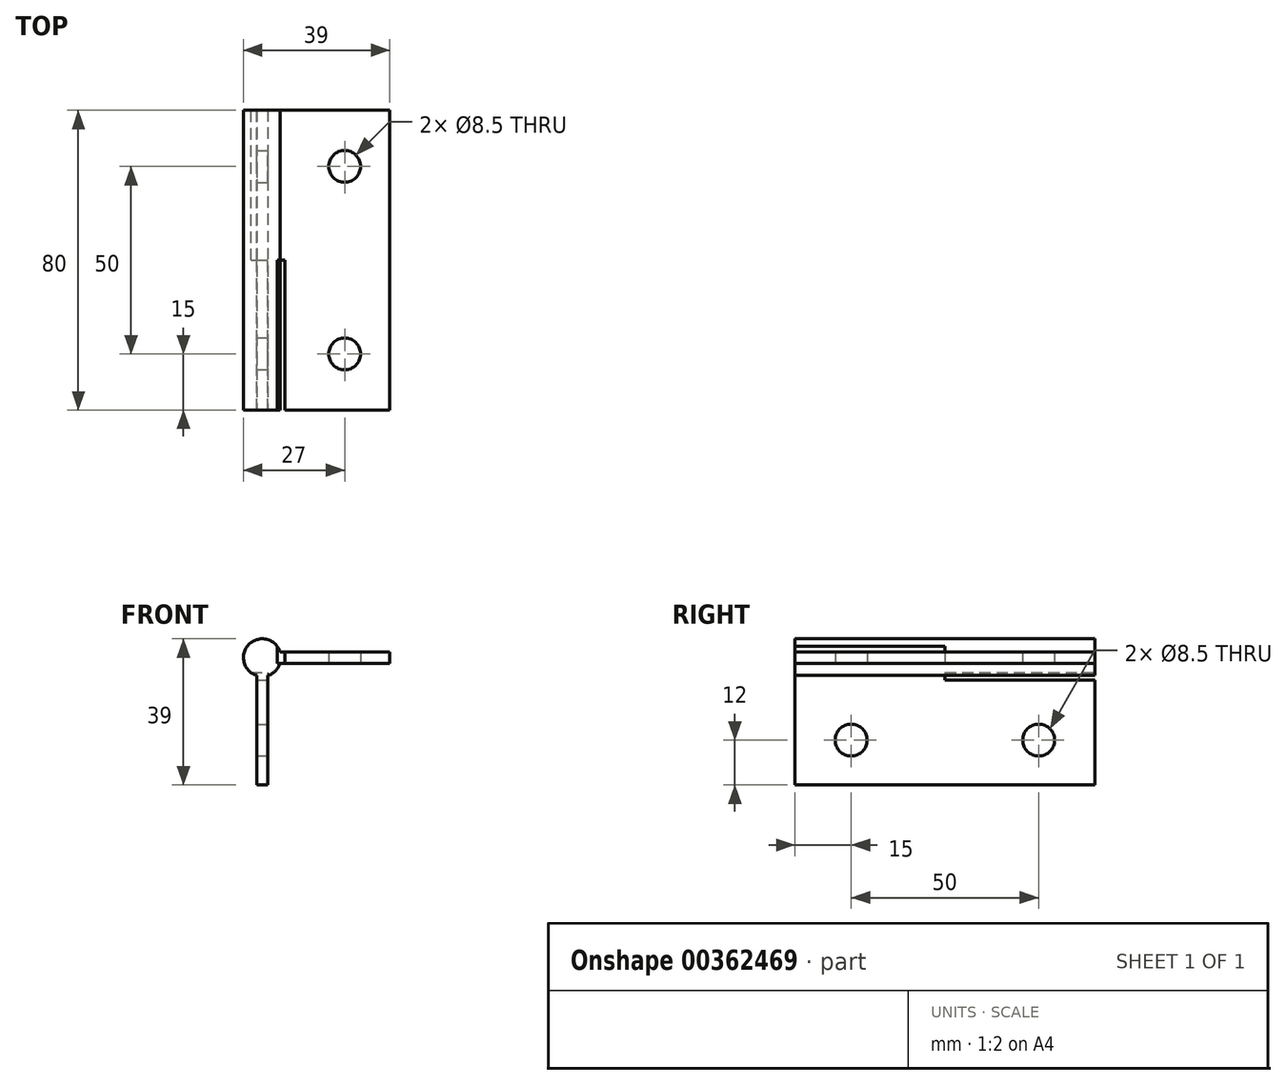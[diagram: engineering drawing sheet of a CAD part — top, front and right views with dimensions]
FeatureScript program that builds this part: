
annotation { "Feature Type Name" : "Feature", "Feature Type Description" : "" }
export const myFeature = defineFeature(function(context is Context, id is Id, definition is map)
    precondition{}
    {
        {
            var Q0;
            Q0=qCreatedBy(makeId("Front.planeOp"),FACE);
            var sketch = newSketch(context, id + "F0", { "sketchPlane" : qUnion([Q0])});
            skCircle(sketch, "E0", {"center": v(0, 0) * mm, "radius": 5 * mm});
            skSolve(sketch);
        }
        {
            var Q0;
            Q0 = qSketchRegion(id + "F0", true);
            extrude(context, id + "F1", {"entities" : qUnion([Q0]), "depth" : 40 * mm, "offsetDistance" : 25 * mm});
        }
        {
            var Q0;
            Q0=qCreatedBy(makeId("Front.planeOp"),FACE);
            var sketch = newSketch(context, id + "F2", { "sketchPlane" : qUnion([Q0])});
            skCircle(sketch, "E1", {"center": v(0, 0) * mm, "radius": 3 * mm});
            skSolve(sketch);
        }
        {
            var Q0;
            Q0 = qSketchRegion(id + "F2", true);
            extrude(context, id + "F3", {"entities" : qUnion([Q0]), "operationType" : NewBodyOperationType.ADD, "oppositeDirection" : true, "depth" : 40 * mm, "offsetDistance" : 25 * mm});
        }
        {
            var Q0;
            Q0=qCreatedBy(makeId("Top.planeOp"),FACE);
            cPlane(context, id + "F4", {"entities" : qUnion([Q0]), "cplaneType" : CPlaneType.OFFSET, "offset" : 4 * mm, "oppositeDirection" : true, "width" : 150 * mm, "height" : 150 * mm});
        }
        {
            var Q0;
            Q0=qCreatedBy(id+"F4.planeOp",FACE);
            var sketch = newSketch(context, id + "F5", { "sketchPlane" : qUnion([Q0])});
            skLineSegment(sketch, "E2.bottom", {"start": v(1.5, 40) * mm, "end": v(-1.5, 40) * mm});
            skLineSegment(sketch, "E2.top", {"start": v(1.5, -40) * mm, "end": v(-1.5, -40) * mm});
            skLineSegment(sketch, "E2.left", {"start": v(1.5, 40) * mm, "end": v(1.5, -40) * mm});
            skLineSegment(sketch, "E2.right", {"start": v(-1.5, 40) * mm, "end": v(-1.5, -40) * mm});
            skPoint(sketch, "E2.middle", {"position": v(0, 0) * mm});
            skSolve(sketch);
        }
        {
            var Q0;
            Q0 = qSketchRegion(id + "F5", true);
            extrude(context, id + "F6", {"entities" : qUnion([Q0]), "operationType" : NewBodyOperationType.ADD, "oppositeDirection" : true, "depth" : 30 * mm, "offsetDistance" : 25 * mm});
        }
        {
            var Q0;
            Q0=qCreatedBy(makeId("Front.planeOp"),FACE);
            var sketch = newSketch(context, id + "F7", { "sketchPlane" : qUnion([Q0])});
            skCircle(sketch, "E3", {"center": v(0, 0) * mm, "radius": 5 * mm});
            skCircle(sketch, "E4", {"center": v(0, 0) * mm, "radius": 3 * mm});
            skSolve(sketch);
        }
        {
            var Q0;
            Q0 = qSketchRegion(id + "F7", true);
            extrude(context, id + "F8", {"entities" : qUnion([Q0]), "oppositeDirection" : true, "depth" : 40 * mm, "offsetDistance" : 25 * mm});
        }
        {
            var Q0;
            Q0=qCreatedBy(makeId("Right.planeOp"),FACE);
            cPlane(context, id + "F9", {"entities" : qUnion([Q0]), "cplaneType" : CPlaneType.OFFSET, "offset" : 4 * mm, "width" : 150 * mm, "height" : 150 * mm});
        }
        {
            var Q0;
            Q0=qCreatedBy(id+"F9.planeOp",FACE);
            var sketch = newSketch(context, id + "F10", { "sketchPlane" : qUnion([Q0])});
            skLineSegment(sketch, "E5.bottom", {"start": v(-40, 1.5) * mm, "end": v(40, 1.5) * mm});
            skLineSegment(sketch, "E5.top", {"start": v(-40, -1.5) * mm, "end": v(40, -1.5) * mm});
            skLineSegment(sketch, "E5.left", {"start": v(-40, 1.5) * mm, "end": v(-40, -1.5) * mm});
            skLineSegment(sketch, "E5.right", {"start": v(40, 1.5) * mm, "end": v(40, -1.5) * mm});
            skPoint(sketch, "E5.middle", {"position": v(0, 0) * mm});
            skSolve(sketch);
        }
        {
            var Q0;
            Q0 = qSketchRegion(id + "F10", true);
            extrude(context, id + "F11", {"entities" : qUnion([Q0]), "operationType" : NewBodyOperationType.ADD, "depth" : 30 * mm, "offsetDistance" : 25 * mm});
        }
        {
            var Q0;
            Q0=makeQuery(id+"F6.opExtrude","SWEPT_FACE",FACE,{"disambiguationData":[OSD([sQuery(id+"F5.wireOp",EDGE,"E2.left")])]});
            var sketch = newSketch(context, id + "F12", { "sketchPlane" : qUnion([Q0])});
            skLineSegment(sketch, "E6.bottom", {"start": v(40, -4) * mm, "end": v(0, -4) * mm});
            skLineSegment(sketch, "E6.top", {"start": v(40, -6) * mm, "end": v(0, -6) * mm});
            skLineSegment(sketch, "E6.left", {"start": v(40, -4) * mm, "end": v(40, -6) * mm});
            skLineSegment(sketch, "E6.right", {"start": v(0, -4) * mm, "end": v(0, -6) * mm});
            skSolve(sketch);
        }
        {
            var Q0;
            Q0 = qSketchRegion(id + "F12", true);
            extrude(context, id + "F13", {"entities" : qUnion([Q0]), "operationType" : NewBodyOperationType.REMOVE, "oppositeDirection" : true, "depth" : 25 * mm, "offsetDistance" : 25 * mm});
        }
        {
            var Q0;
            Q0=makeQuery(id+"F11.opExtrude","SWEPT_FACE",FACE,{"disambiguationData":[OSD([sQuery(id+"F10.wireOp",EDGE,"E5.top")])]});
            var sketch = newSketch(context, id + "F14", { "sketchPlane" : qUnion([Q0])});
            skLineSegment(sketch, "E7.bottom", {"start": v(4, 40) * mm, "end": v(6, 40) * mm});
            skLineSegment(sketch, "E7.top", {"start": v(4, 0) * mm, "end": v(6, 0) * mm});
            skLineSegment(sketch, "E7.left", {"start": v(4, 40) * mm, "end": v(4, 0) * mm});
            skLineSegment(sketch, "E7.right", {"start": v(6, 40) * mm, "end": v(6, 0) * mm});
            skSolve(sketch);
        }
        {
            var Q0;
            Q0 = qSketchRegion(id + "F14", true);
            extrude(context, id + "F15", {"entities" : qUnion([Q0]), "operationType" : NewBodyOperationType.REMOVE, "oppositeDirection" : true, "depth" : 25 * mm, "offsetDistance" : 25 * mm});
        }
        {
            var Q0;
            Q0=makeQuery(id+"F11.opExtrude","SWEPT_FACE",FACE,{"disambiguationData":[OSD([sQuery(id+"F10.wireOp",EDGE,"E5.top")])]});
            var sketch = newSketch(context, id + "F16", { "sketchPlane" : qUnion([Q0])});
            skCircle(sketch, "E8", {"center": v(22, 25) * mm, "radius": 4.25 * mm});
            skCircle(sketch, "E9.MirrorC", {"center": v(22, -25) * mm, "radius": 4.25 * mm});
            skSolve(sketch);
        }
        {
            var Q0;
            Q0 = qSketchRegion(id + "F16", true);
            extrude(context, id + "F17", {"entities" : qUnion([Q0]), "operationType" : NewBodyOperationType.REMOVE, "oppositeDirection" : true, "depth" : 25 * mm, "offsetDistance" : 25 * mm});
        }
        {
            var Q0;
            Q0=makeQuery(id+"F6.opExtrude","SWEPT_FACE",FACE,{"disambiguationData":[OSD([sQuery(id+"F5.wireOp",EDGE,"E2.left")])]});
            var sketch = newSketch(context, id + "F18", { "sketchPlane" : qUnion([Q0])});
            skCircle(sketch, "E10", {"center": v(-25, -22) * mm, "radius": 4.25 * mm});
            skCircle(sketch, "E11.MirrorC", {"center": v(25, -22) * mm, "radius": 4.25 * mm});
            skSolve(sketch);
        }
        {
            var Q0;
            Q0 = qSketchRegion(id + "F18", true);
            extrude(context, id + "F19", {"entities" : qUnion([Q0]), "operationType" : NewBodyOperationType.REMOVE, "oppositeDirection" : true, "depth" : 25 * mm, "offsetDistance" : 25 * mm});
        }
    });
